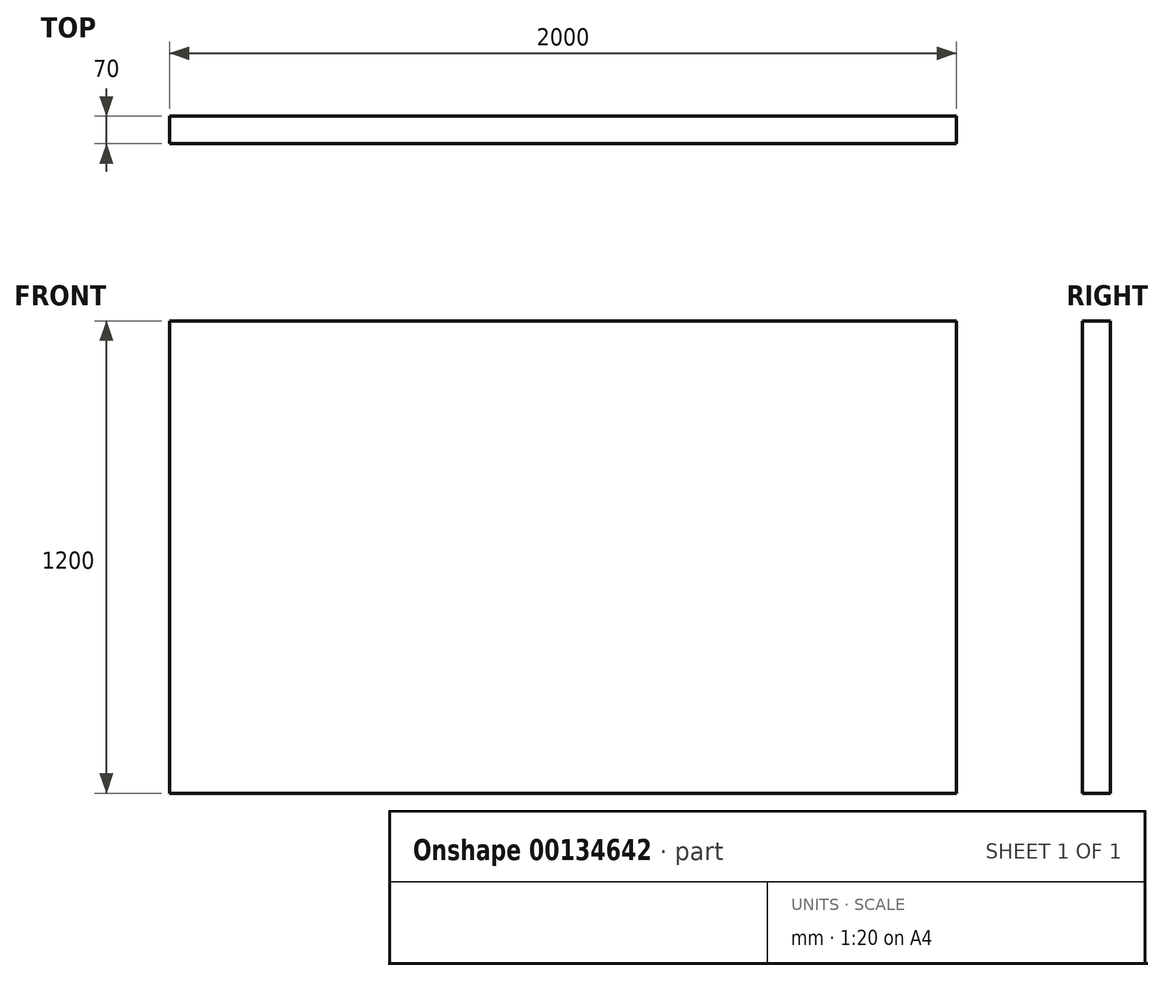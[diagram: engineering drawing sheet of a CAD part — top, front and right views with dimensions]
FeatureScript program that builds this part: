
annotation { "Feature Type Name" : "Feature", "Feature Type Description" : "" }
export const myFeature = defineFeature(function(context is Context, id is Id, definition is map)
    precondition{}
    {
        {
            var Q0;
            Q0=qCreatedBy(makeId("Top.planeOp"),FACE);
            var sketch = newSketch(context, id + "F0", { "sketchPlane" : qUnion([Q0])});
            skLineSegment(sketch, "E0.bottom", {"start": v(1000, -35) * mm, "end": v(-1000, -35) * mm});
            skLineSegment(sketch, "E0.top", {"start": v(1000, 35) * mm, "end": v(-1000, 35) * mm});
            skLineSegment(sketch, "E0.left", {"start": v(1000, -35) * mm, "end": v(1000, 35) * mm});
            skLineSegment(sketch, "E0.right", {"start": v(-1000, -35) * mm, "end": v(-1000, 35) * mm});
            skPoint(sketch, "E0.middle", {"position": v(0, 0) * mm});
            skSolve(sketch);
        }
        {
            var Q0;
            Q0=makeQuery(id+"F0.imprint","IMPRINT",FACE,{"disambiguationData":[TD([[makeQuery(id+"F0.imprint","IMPRINT",EDGE,{"derivedFrom":sQuery(id+"F0.wireOp",EDGE,"E0.bottom")}),-1.0]])]});
            extrude(context, id + "F1", {"entities" : qUnion([Q0]), "depth" : 1200 * mm});
        }
    });
